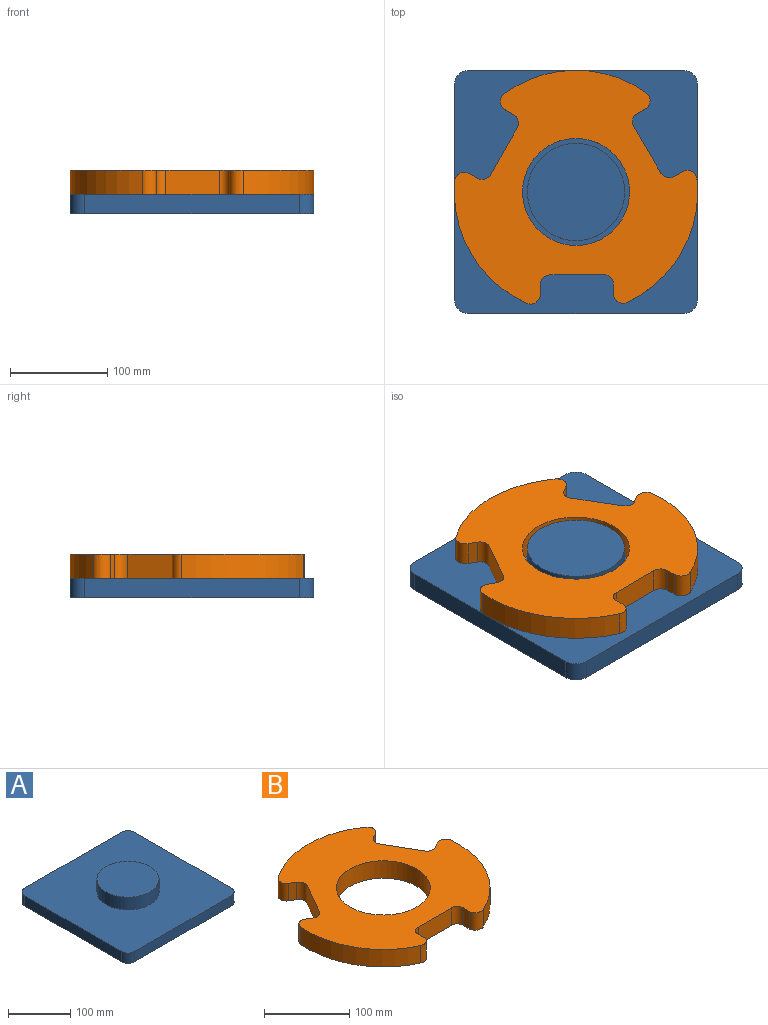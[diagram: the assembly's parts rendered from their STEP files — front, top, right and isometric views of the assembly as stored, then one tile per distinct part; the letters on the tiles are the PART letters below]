
ASSEMBLY  parts=2 mates=1
PART A: 12 faces, bbox 250x250x45 mm
  f0: plane 220x20mm, normal (1,0,0), area 4400mm2, adj f4,f5,f8,f11
  f1: plane 220x20mm, normal (0,1,0), area 4400mm2, adj f4,f5,f8,f9
  f2: plane 220x20mm, normal (-1,0,0), area 4400mm2, adj f4,f5,f9,f10
  f3: plane 220x20mm, normal (0,-1,0), area 4400mm2, adj f4,f5,f10,f11
  f4: plane 250x250mm, normal (0,0,1), area 54452.9mm2, adj f0,f1,f2,f3,f6,f8,f9,f10
  f5: plane 250x250mm, normal (0,0,-1), area 62306.9mm2, adj f0,f1,f2,f3,f8,f9,f10,f11
  f6: cylinder r=50mm len=100mm, axis (0,0,-1), area 7854mm2, adj f4,f7
  f7: plane 100x100mm, normal (0,0,1), area 7854mm2, adj f6
  f8: cylinder r=15mm len=20mm, axis (0,0,-1), area 471.2mm2, adj f0,f1,f4,f5
  f9: cylinder r=15mm len=20mm, axis (0,0,1), area 471.2mm2, adj f1,f2,f4,f5
  f10: cylinder r=15mm len=20mm, axis (0,0,-1), area 471.2mm2, adj f2,f3,f4,f5
  f11: cylinder r=15mm len=20mm, axis (0,0,1), area 471.2mm2, adj f0,f3,f4,f5
PART B: 27 faces, bbox 250x239.7x25 mm
  f0: plane 250x239.73mm, normal (0,0,1), area 30837.4mm2, adj f2,f3,f4,f5,f6,f7,f8,f9
  f1: plane 250x239.73mm, normal (0,0,-1), area 30837.4mm2, adj f2,f3,f4,f5,f6,f7,f8,f9
  f2: cylinder r=125mm len=145.54mm, axis (0,0,-1), area 3883.8mm2, adj f0,f1,f18,f26
  f3: cylinder r=125mm len=126.05mm, axis (0,0,-1), area 3883.8mm2, adj f0,f1,f11,f19
  f4: cylinder r=55mm len=110mm, axis (0,0,-1), area 8639.4mm2, adj f0,f1
  f5: cylinder r=125mm len=126.05mm, axis (0,0,-1), area 3883.8mm2, adj f0,f1,f12,f25
  f6: plane 25x9.73mm, normal (-1,0,0), area 243.3mm2, adj f0,f1,f9,f12
  f7: plane 55x25mm, normal (0,-1,0), area 1375mm2, adj f0,f1,f9,f10
  f8: plane 25x9.73mm, normal (1,0,0), area 243.3mm2, adj f0,f1,f10,f11
  f9: cylinder r=10mm len=25mm, axis (0,0,-1), area 392.7mm2, adj f0,f1,f6,f7
  f10: cylinder r=10mm len=25mm, axis (0,0,-1), area 392.7mm2, adj f0,f1,f7,f8
  f11: cylinder r=10mm len=25mm, axis (0,0,-1), area 499.1mm2, adj f0,f1,f3,f8
  f12: cylinder r=10mm len=25mm, axis (0,0,-1), area 499.1mm2, adj f0,f1,f5,f6
  f13: plane 25x8.43mm, normal (0.5,0.87,0), area 243.3mm2, adj f0,f1,f16,f19
  f14: plane 47.63x27.5mm, normal (-0.87,0.5,0), area 1375mm2, adj f0,f1,f16,f17
  f15: plane 25x8.43mm, normal (-0.5,-0.87,0), area 243.3mm2, adj f0,f1,f17,f18
  f16: cylinder r=10mm len=25mm, axis (0,0,-1), area 392.7mm2, adj f0,f1,f13,f14
  f17: cylinder r=10mm len=25mm, axis (0,0,-1), area 392.7mm2, adj f0,f1,f14,f15
  f18: cylinder r=10mm len=25mm, axis (0,0,-1), area 499.1mm2, adj f0,f1,f2,f15
  f19: cylinder r=10mm len=25mm, axis (0,0,-1), area 499.1mm2, adj f0,f1,f3,f13
  f20: plane 25x8.43mm, normal (0.5,-0.87,0), area 243.3mm2, adj f0,f1,f23,f26
  f21: plane 47.63x27.5mm, normal (0.87,0.5,0), area 1375mm2, adj f0,f1,f23,f24
  f22: plane 25x8.43mm, normal (-0.5,0.87,0), area 243.3mm2, adj f0,f1,f24,f25
  f23: cylinder r=10mm len=25mm, axis (0,0,-1), area 392.7mm2, adj f0,f1,f20,f21
  f24: cylinder r=10mm len=25mm, axis (0,0,-1), area 392.7mm2, adj f0,f1,f21,f22
  f25: cylinder r=10mm len=25mm, axis (0,0,-1), area 499.1mm2, adj f0,f1,f5,f22
  f26: cylinder r=10mm len=25mm, axis (0,0,-1), area 499.1mm2, adj f0,f1,f2,f20
PLACE A at identity fixed
PLACE B rot(axis=(0,0,1),120.5deg) t=(0,0,0)mm
MATE revolute A.f6 <-> B.f2  axis (0,0,1) through (0,0,45)mm
